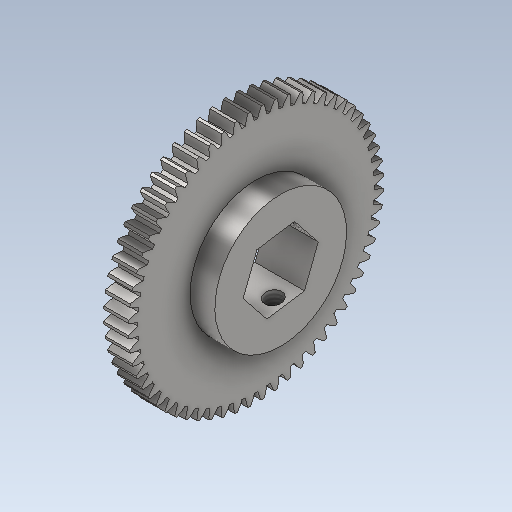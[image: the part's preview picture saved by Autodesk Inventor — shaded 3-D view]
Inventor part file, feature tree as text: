
AUTODESK INVENTOR PART (.ipt)
format: ipt  version: 2023 (Build 270158000, 158)  size: 1,101,824 bytes
history: native  units: in
note: dims shown in document units (in); Inventor stores cm internally (conversion verified against a paired STEP export)
features: sketch x3, extrude x1, revolve x1, hole x1, projected_geometry x1, other x1
ambient origin geometry x8: Origin, YZ Plane, XZ Plane, XY Plane, X Axis, Y Axis, Z Axis, Center Point
bodies: Solid1 (feature_tree)
feature tree (8):
  extrude  "Extrusion4"  Depth=0.1875in
  revolve  "Revolution1"  [1 undecoded]
  hole  "Hole2"  [1 undecoded]
  sketch  "Sketch6"  dims[d23=0.1875in d26=2.4724in]
  sketch  "Sketch7"  dims[d27=0.5in d28=0.0in d29=0.0in]
  sketch  "Sketch8"  dims[d30=0.5in d31=0.1875in d32=0.13in d33=0.328in d34=0.375in d35=0.25in d36=0.5635in d37=0.302in d38=0.8108in d39=0.0in d40=0.0in d41=0.0in d42=0.0in]
  projected_geometry  "Projected Loop1"
  other  "TeethCuts"
note: 2 required parameter values undecoded (feature->parameter linkage not recoverable at this tier; creation-order binding heuristic only, values carry confidence <= 0.55)